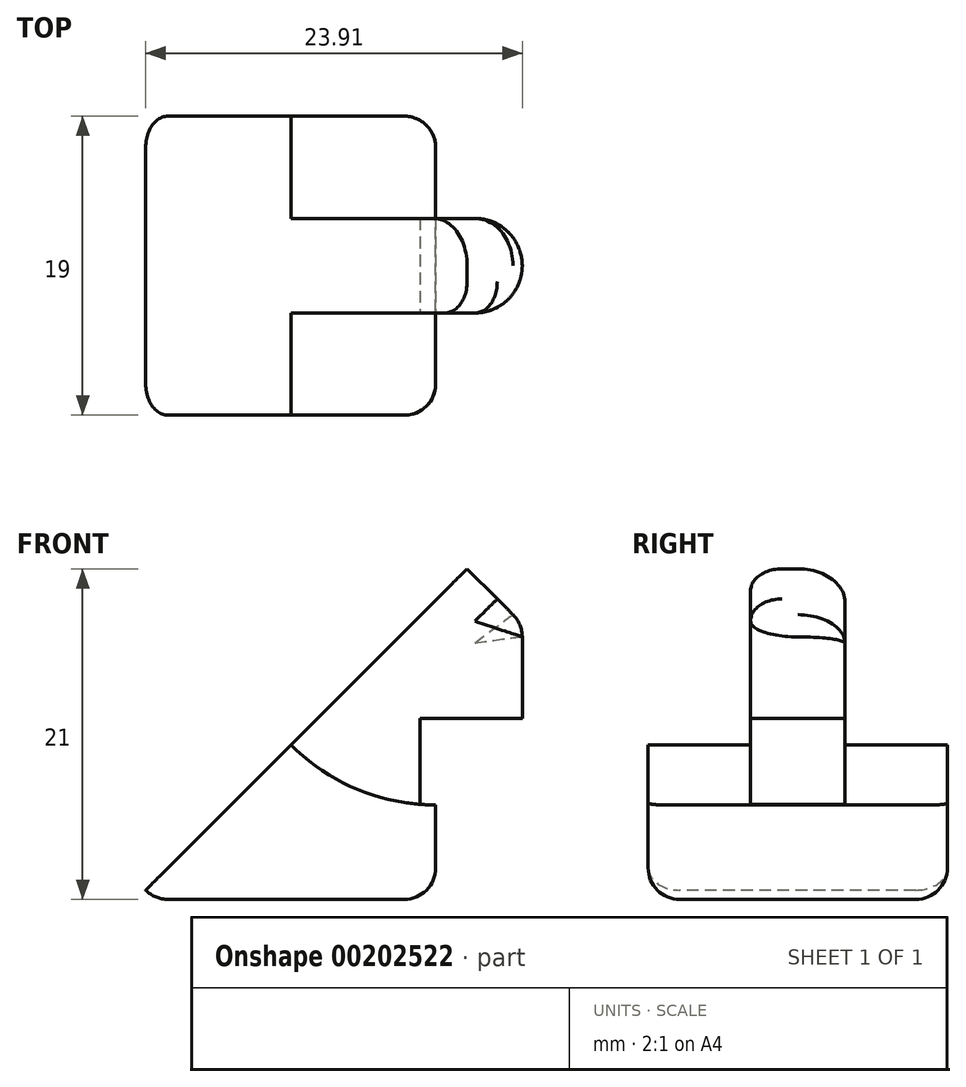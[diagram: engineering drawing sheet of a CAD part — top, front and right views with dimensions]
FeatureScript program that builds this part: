
annotation { "Feature Type Name" : "Feature", "Feature Type Description" : "" }
export const myFeature = defineFeature(function(context is Context, id is Id, definition is map)
    precondition{}
    {
        {
            var Q0;
            Q0=qCreatedBy(makeId("Front.planeOp"),FACE);
            var sketch = newSketch(context, id + "F0", { "sketchPlane" : qUnion([Q0])});
            skLineSegment(sketch, "E0.bottom", {"start": v(0, 0) * mm, "end": v(19, 0) * mm});
            skLineSegment(sketch, "E0.top", {"start": v(0, 19) * mm, "end": v(19, 19) * mm});
            skLineSegment(sketch, "E0.left", {"start": v(0, 0) * mm, "end": v(0, 19) * mm});
            skLineSegment(sketch, "E0.right", {"start": v(19, 0) * mm, "end": v(19, 19) * mm});
            skSolve(sketch);
        }
        {
            var Q0;
            Q0=qSketchRegion(id+"F0",true);
            extrude(context, id + "F1", {"entities" : qUnion([Q0]), "depth" : 19 * mm, "symmetric" : true});
        }
        {
            var Q0;
            Q0=makeQuery(id+"F1.opExtrude","CAP_FACE",FACE,{"disambiguationData":[OSD([sQuery(id+"F0.wireOp",EDGE,"E0.bottom"),sQuery(id+"F0.wireOp",EDGE,"E0.top"),sQuery(id+"F0.wireOp",EDGE,"E0.left"),sQuery(id+"F0.wireOp",EDGE,"E0.right")])],"isStart":false});
            var sketch = newSketch(context, id + "F2", { "sketchPlane" : qUnion([Q0])});
            skArc(sketch, "E1", {"start": v(19, 6) * mm, "mid": v(9.8, 9.8) * mm, "end": v(6, 19) * mm});
            skLineSegment(sketch, "E2", {"start": v(19, 6) * mm, "end": v(19, 19) * mm});
            skLineSegment(sketch, "E3", {"start": v(6, 19) * mm, "end": v(19, 19) * mm});
            skSolve(sketch);
        }
        {
            var Q0;
            Q0=qSketchRegion(id+"F2",true);
            extrude(context, id + "F3", {"entities" : qUnion([Q0]), "operationType" : NewBodyOperationType.REMOVE, "endBound" : BoundingType.THROUGH_ALL, "oppositeDirection" : true, "depth" : 25 * mm});
        }
        {
            var Q0;
            Q0=qCreatedBy(makeId("Front.planeOp"),FACE);
            var sketch = newSketch(context, id + "F4", { "sketchPlane" : qUnion([Q0])});
            skLineSegment(sketch, "E4", {"start": v(0, 0) * mm, "end": v(0, 18) * mm});
            skLineSegment(sketch, "E5", {"start": v(0, 18) * mm, "end": v(11.5, 18) * mm});
            skLineSegment(sketch, "E6", {"start": v(11.5, 18) * mm, "end": v(11.5, 24.5) * mm});
            skLineSegment(sketch, "E7", {"start": v(11.5, 24.5) * mm, "end": v(24.5, 24.5) * mm});
            skLineSegment(sketch, "E8", {"start": v(24.5, 24.5) * mm, "end": v(24.5, 11.5) * mm});
            skLineSegment(sketch, "E9", {"start": v(24.5, 11.5) * mm, "end": v(18, 11.5) * mm});
            skLineSegment(sketch, "E10", {"start": v(18, 11.5) * mm, "end": v(18, 0) * mm});
            skLineSegment(sketch, "E11", {"start": v(18, 0) * mm, "end": v(0, 0) * mm});
            skSolve(sketch);
        }
        {
            var Q0;
            Q0=qSketchRegion(id+"F4",true);
            extrude(context, id + "F5", {"entities" : qUnion([Q0]), "operationType" : NewBodyOperationType.ADD, "depth" : 6 * mm, "symmetric" : true});
        }
        {
            var Q0;
            Q0=makeQuery(id+"F1.opExtrude","SWEPT_EDGE",EDGE,{"disambiguationData":[OSD([sQuery(id+"F0.wireOp",EDGE,"E0.bottom"),sQuery(id+"F0.wireOp",EDGE,"E0.left")])]});
            fillet(context, id + "F6", {"entities" : qUnion([Q0]), "radius" : 2 * mm, "tangentPropagation" : true, "allowEdgeOverflow" : false});
        }
        {
            var Q0;
            Q0=makeQuery(id+"F5.opExtrude","CAP_FACE",FACE,{"disambiguationData":[OSD([sQuery(id+"F4.wireOp",EDGE,"E4"),sQuery(id+"F4.wireOp",EDGE,"E5"),sQuery(id+"F4.wireOp",EDGE,"E6"),sQuery(id+"F4.wireOp",EDGE,"E7"),sQuery(id+"F4.wireOp",EDGE,"E8"),sQuery(id+"F4.wireOp",EDGE,"E9"),sQuery(id+"F4.wireOp",EDGE,"E10"),sQuery(id+"F4.wireOp",EDGE,"E11")])],"isStart":false});
            var sketch = newSketch(context, id + "F7", { "sketchPlane" : qUnion([Q0])});
            skLineSegment(sketch, "E12", {"start": v(24.5, 11.5) * mm, "end": v(24.5, 17.5) * mm});
            skLineSegment(sketch, "E13", {"start": v(24.5, 17.5) * mm, "end": v(17.5, 24.5) * mm});
            skLineSegment(sketch, "E14", {"start": v(17.5, 24.5) * mm, "end": v(11.5, 24.5) * mm});
            skLineSegment(sketch, "E15", {"start": v(11.5, 24.5) * mm, "end": v(11.5, 11.5) * mm});
            skLineSegment(sketch, "E16", {"start": v(11.5, 11.5) * mm, "end": v(24.5, 11.5) * mm});
            skLineSegment(sketch, "E17", {"start": v(24.5, 17.5) * mm, "end": v(24.5, 24.5) * mm});
            skLineSegment(sketch, "E18", {"start": v(24.5, 24.5) * mm, "end": v(17.5, 24.5) * mm});
            skSolve(sketch);
        }
        {
            var Q0;
            Q0=makeQuery(id+"F7.imprint","IMPRINT",FACE,{"disambiguationData":[TD([[makeQuery(id+"F7.imprint","IMPRINT",EDGE,{"derivedFrom":sQuery(id+"F7.wireOp",EDGE,"E13")}),-1.0]])]});
            extrude(context, id + "F8", {"entities" : qUnion([Q0]), "operationType" : NewBodyOperationType.REMOVE, "endBound" : BoundingType.THROUGH_ALL, "oppositeDirection" : true, "depth" : 25 * mm});
        }
        {
            var Q0;
            Q0=makeQuery(id+"F1.opExtrude","CAP_EDGE",EDGE,{"disambiguationData":[OSD([sQuery(id+"F0.wireOp",EDGE,"E0.left")])],"isStart":false});
            var Q1;
            Q1=makeQuery(id+"F1.opExtrude","CAP_EDGE",EDGE,{"disambiguationData":[OSD([sQuery(id+"F0.wireOp",EDGE,"E0.left")])],"isStart":true});
            var Q2;
            Q2=makeQuery(id+"F1.opExtrude","SWEPT_EDGE",EDGE,{"disambiguationData":[OSD([sQuery(id+"F0.wireOp",EDGE,"E0.top"),sQuery(id+"F0.wireOp",EDGE,"E0.left")])]});
            var Q3;
            Q3=makeQuery(id+"F1.opExtrude","CAP_EDGE",EDGE,{"disambiguationData":[OSD([sQuery(id+"F0.wireOp",EDGE,"E0.top")])],"isStart":true});
            var Q4;
            Q4=makeQuery(id+"F1.opExtrude","CAP_EDGE",EDGE,{"disambiguationData":[OSD([sQuery(id+"F0.wireOp",EDGE,"E0.top")])],"isStart":false});
            var Q5;
            Q5=makeQuery(id+"F1.opExtrude","CAP_EDGE",EDGE,{"disambiguationData":[OSD([sQuery(id+"F0.wireOp",EDGE,"E0.right")])],"isStart":true});
            var Q6;
            Q6=makeQuery(id+"F1.opExtrude","SWEPT_EDGE",EDGE,{"disambiguationData":[OSD([sQuery(id+"F0.wireOp",EDGE,"E0.bottom"),sQuery(id+"F0.wireOp",EDGE,"E0.right")])]});
            var Q7;
            Q7=makeQuery(id+"F1.opExtrude","CAP_EDGE",EDGE,{"disambiguationData":[OSD([sQuery(id+"F0.wireOp",EDGE,"E0.right")])],"isStart":false});
            fillet(context, id + "F9", {"entities" : qUnion([Q0, Q1, Q2, Q3, Q4, Q5, Q6, Q7]), "radius" : 2 * mm, "tangentPropagation" : true, "allowEdgeOverflow" : false});
        }
        {
            var Q0;
            Q0=qCreatedBy(makeId("Front.planeOp"),FACE);
            var sketch = newSketch(context, id + "F10", { "sketchPlane" : qUnion([Q0])});
            skLineSegment(sketch, "E19", {"start": v(0, 0) * mm, "end": v(25, 25) * mm});
            skLineSegment(sketch, "E20", {"start": v(25, 25) * mm, "end": v(0, 25) * mm});
            skLineSegment(sketch, "E21", {"start": v(0, 25) * mm, "end": v(0, 0) * mm});
            skSolve(sketch);
        }
        {
            var Q0;
            Q0 = qSketchRegion(id + "F10", true);
            extrude(context, id + "F11", {"entities" : qUnion([Q0]), "operationType" : NewBodyOperationType.REMOVE, "oppositeDirection" : true, "depth" : 19 * mm, "symmetric" : true});
        }
        {
            var Q0;
            Q0=makeQuery(id+"F8.boolean.opBoolean","COPY",EDGE,{"derivedFrom":makeQuery(id+"F8.opExtrude","CAP_EDGE",EDGE,{"disambiguationData":[OSD([sQuery(id+"F7.wireOp",EDGE,"E13")])],"isStart":true})});
            var Q1;
            Q1=makeQuery(id+"F5.opExtrude","CAP_EDGE",EDGE,{"disambiguationData":[OSD([sQuery(id+"F4.wireOp",EDGE,"E8")])],"isStart":false});
            var Q2;
            Q2=makeQuery(id+"F5.opExtrude","CAP_EDGE",EDGE,{"disambiguationData":[OSD([sQuery(id+"F4.wireOp",EDGE,"E8")])],"isStart":true});
            var Q3;
            Q3=makeQuery(id+"F8.boolean.opBoolean","INTERSECT",EDGE,{"derivedFrom":[makeQuery(id+"F5.opExtrude","CAP_FACE",FACE,{"disambiguationData":[OSD([sQuery(id+"F4.wireOp",EDGE,"E4"),sQuery(id+"F4.wireOp",EDGE,"E5"),sQuery(id+"F4.wireOp",EDGE,"E6"),sQuery(id+"F4.wireOp",EDGE,"E7"),sQuery(id+"F4.wireOp",EDGE,"E8"),sQuery(id+"F4.wireOp",EDGE,"E9"),sQuery(id+"F4.wireOp",EDGE,"E10"),sQuery(id+"F4.wireOp",EDGE,"E11")])],"isStart":true}),makeQuery(id+"F8.opExtrude","SWEPT_FACE",FACE,{"disambiguationData":[OSD([sQuery(id+"F7.wireOp",EDGE,"E13")])]})]});
            fillet(context, id + "F12", {"entities" : qUnion([Q0, Q1, Q2, Q3]), "radius" : 3 * mm, "tangentPropagation" : true, "allowEdgeOverflow" : false});
        }
        {
            var Q0;
            {var subQ0=sQuery(id+"F4.wireOp",EDGE,"E8");Q0=makeQuery(id+"F12.opFillet","BLEND_EDGE",EDGE,{"blendedFrom":[makeQuery(id+"F5.opExtrude","CAP_EDGE",EDGE,{"disambiguationData":[OSD([subQ0])],"isStart":true}),makeQuery(id+"F8.boolean.opBoolean","INTERSECT",EDGE,{"derivedFrom":[makeQuery(id+"F5.opExtrude","CAP_FACE",FACE,{"disambiguationData":[OSD([sQuery(id+"F4.wireOp",EDGE,"E4"),sQuery(id+"F4.wireOp",EDGE,"E5"),sQuery(id+"F4.wireOp",EDGE,"E6"),sQuery(id+"F4.wireOp",EDGE,"E7"),subQ0,sQuery(id+"F4.wireOp",EDGE,"E9"),sQuery(id+"F4.wireOp",EDGE,"E10"),sQuery(id+"F4.wireOp",EDGE,"E11")])],"isStart":true}),makeQuery(id+"F8.opExtrude","SWEPT_FACE",FACE,{"disambiguationData":[OSD([sQuery(id+"F7.wireOp",EDGE,"E13")])]})]})],"blendedInto":[]});}
            fillet(context, id + "F13", {"entities" : qUnion([Q0]), "radius" : 2 * mm, "tangentPropagation" : true, "allowEdgeOverflow" : false});
        }
    });
